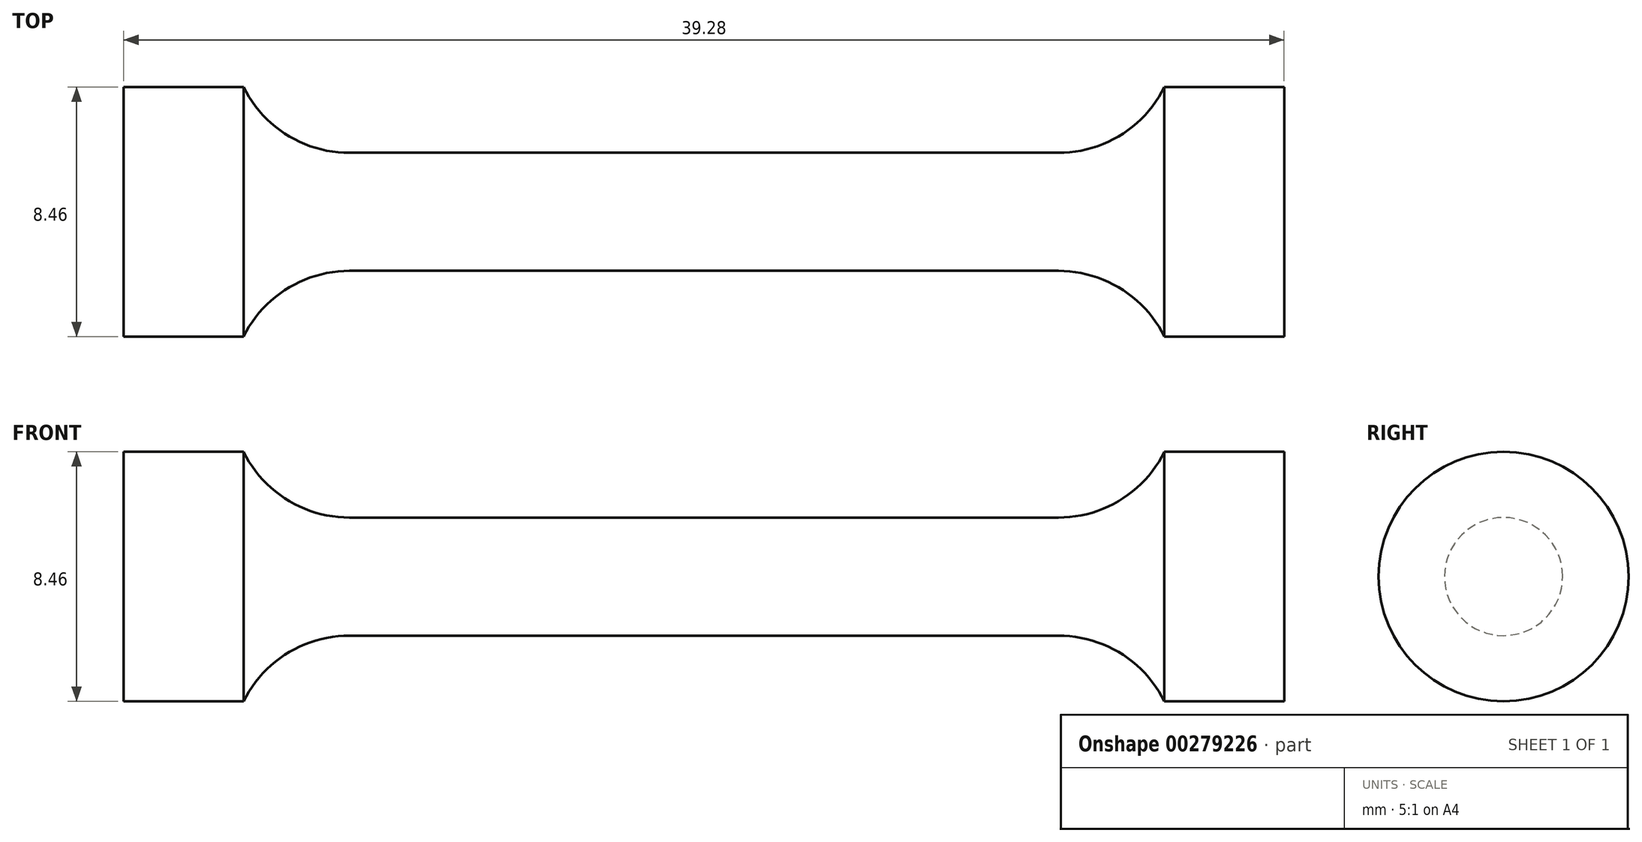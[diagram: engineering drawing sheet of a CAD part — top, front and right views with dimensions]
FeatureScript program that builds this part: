
annotation { "Feature Type Name" : "Feature", "Feature Type Description" : "" }
export const myFeature = defineFeature(function(context is Context, id is Id, definition is map)
    precondition{}
    {
        {
            var Q0;
            Q0=qCreatedBy(makeId("Front.planeOp"),FACE);
            var sketch = newSketch(context, id + "F0", { "sketchPlane" : qUnion([Q0])});
            skLineSegment(sketch, "E0", {"start": v(0, 2) * mm, "end": v(12, 2) * mm});
            skArc(sketch, "E1", {"start": v(12, 2) * mm, "mid": v(14.11, 2.6) * mm, "end": v(15.59, 4.23) * mm});
            skLineSegment(sketch, "E2", {"start": v(15.59, 4.23) * mm, "end": v(19.64, 4.23) * mm});
            skLineSegment(sketch, "E3", {"start": v(19.64, 4.23) * mm, "end": v(19.64, 0) * mm});
            skLineSegment(sketch, "E4.MirrorCS", {"start": v(0, 2) * mm, "end": v(-12, 2) * mm});
            skLineSegment(sketch, "E5.MirrorCS", {"start": v(-19.64, 4.23) * mm, "end": v(-19.64, 0) * mm});
            skLineSegment(sketch, "E6.MirrorCS", {"start": v(-15.59, 4.23) * mm, "end": v(-19.64, 4.23) * mm});
            skArc(sketch, "E7.MirrorCS", {"start": v(-12, 2) * mm, "mid": v(-14.11, 2.6) * mm, "end": v(-15.59, 4.23) * mm});
            skLineSegment(sketch, "E8", {"start": v(-19.64, 0) * mm, "end": v(19.64, 0) * mm});
            skSolve(sketch);
        }
        {
            var Q0;
            Q0 = qSketchRegion(id + "F0", true);
            var Q1;
            Q1=sQuery(id+"F0.wireOp",EDGE,"E8");
            revolve(context, id + "F1", {"entities" : qUnion([Q0]), "axis" : qUnion([Q1]), "revolveType" : RevolveType.FULL});
        }
    });
